# Revit family: ARFX16
name_source: partatom
category: Lighting Fixtures
revit_build: Autodesk Revit 2013 (Build: 20130531_2115(x64)
units: mm (PartAtom-declared; Revit-internal decimal feet)

## types (7) — shared parameters
Apparent Load = 0 VA
Assembly Code = D5020200
Color Filter = 16777215
Default Elevation = 48"
Description = ArcheType®Flood Luminaire
Dimming Lamp Color Temperature Shift = <None>
Emit Shape Visible in Rendering = No
Emit from Rectangle Length = 13"
Emit from Rectangle Width = 13"
Glass Finish = Hubbell - Glass
Lamp = LED
Load Classification = Lighting
Manufacturer = Kim Lighting
Manufacturer Fax = 626-369-2695
Model = ARFX16
Photometric Notes = More IES files download on Photometric Web Link
Photometric Web File = ARFX16MF-3K50.IES
Photometric Web Link = http://www.kimlighting.com
Power Factor = 1
Product Documentation Link = http://www.kimlighting.com
Product Page URL = http://www.kimlighting.com
Tilt Angle = 90.00°
URL = http://www.kimlighting.com
Voltage = 120 V
Wattage Comments = 110W to 211W

## per-type parameters (varying)
| type | Finish |
| Light Gray | Powdercoat - Hubbell - Light Gray |
| Black | Powdercoat - Hubbell - Black |
| Dark Bronze | Powdercoat - Hubbell - Dark Bronze |
| Graphite | Powdercoat - Hubbell - Graphite |
| Platinum Silver | Powdercoat - Hubbell - Platinum |
| Titanium | Powdercoat - Hubbell - Titanium |
| White | Powdercoat - Hubbell - White |

## geometry (parser evidence)
native form markers: Blend x1, Sweep x1
no freeform markers — native parametric forms only
